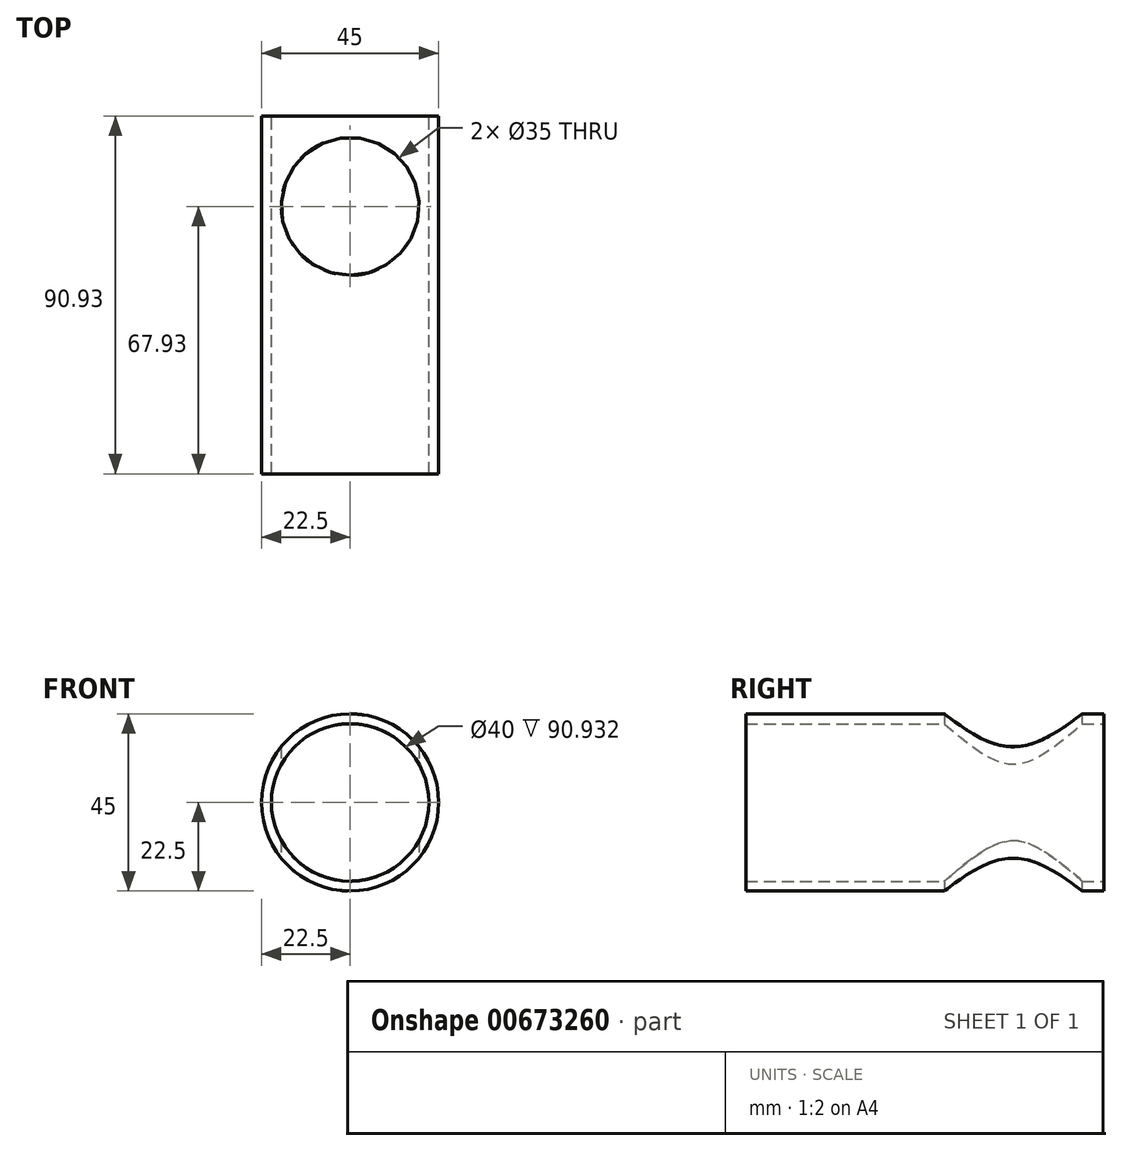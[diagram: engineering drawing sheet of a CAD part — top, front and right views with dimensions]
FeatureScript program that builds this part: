
annotation { "Feature Type Name" : "Feature", "Feature Type Description" : "" }
export const myFeature = defineFeature(function(context is Context, id is Id, definition is map)
    precondition{}
    {
        {
            var Q0;
            Q0=qCreatedBy(makeId("Front.planeOp"),FACE);
            var sketch = newSketch(context, id + "F0", { "sketchPlane" : qUnion([Q0])});
            skCircle(sketch, "E0", {"center": v(0, 0) * mm, "radius": 22.5 * mm});
            skCircle(sketch, "E1", {"center": v(0, 0) * mm, "radius": 20 * mm});
            skSolve(sketch);
        }
        {
            var Q0;
            Q0 = qSketchRegion(id + "F0", true);
            extrude(context, id + "F1", {"entities" : qUnion([Q0]), "depth" : 90.93 * mm, "offsetDistance" : 25.4 * mm});
        }
        {
            var Q0;
            Q0=qCreatedBy(makeId("Top.planeOp"),FACE);
            var sketch = newSketch(context, id + "F2", { "sketchPlane" : qUnion([Q0])});
            skCircle(sketch, "E2", {"center": v(0, -23) * mm, "radius": 17.5 * mm});
            skSolve(sketch);
        }
        {
            var Q0;
            Q0 = qSketchRegion(id + "F2", true);
            extrude(context, id + "F3", {"entities" : qUnion([Q0]), "operationType" : NewBodyOperationType.REMOVE, "depth" : 25 * mm, "offsetDistance" : 25 * mm, "hasSecondDirection" : true, "secondDirectionBound" : SecondDirectionBoundingType.THROUGH_ALL, "secondDirectionOppositeDirection" : true, "secondDirectionDepth" : 25 * mm});
        }
    });
